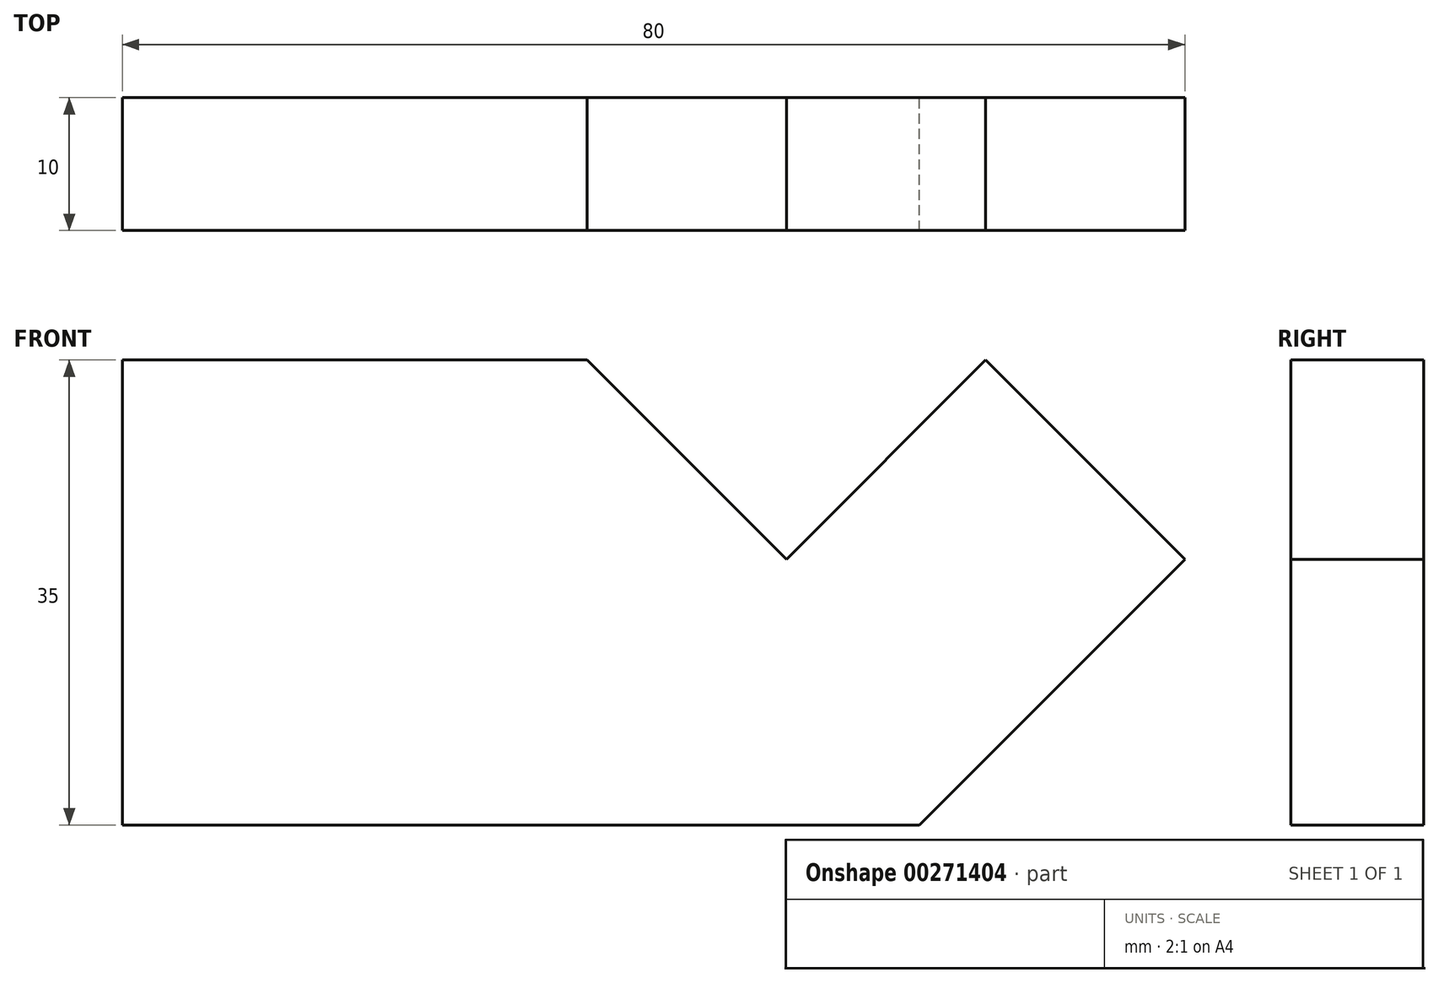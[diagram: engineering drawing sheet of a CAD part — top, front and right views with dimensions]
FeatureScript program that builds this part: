
annotation { "Feature Type Name" : "Feature", "Feature Type Description" : "" }
export const myFeature = defineFeature(function(context is Context, id is Id, definition is map)
    precondition{}
    {
        {
            var Q0;
            Q0=qCreatedBy(makeId("Front.planeOp"),FACE);
            var sketch = newSketch(context, id + "F0", { "sketchPlane" : qUnion([Q0])});
            skLineSegment(sketch, "E0", {"start": v(0, 0) * mm, "end": v(0, 35) * mm});
            skLineSegment(sketch, "E1", {"start": v(0, 0) * mm, "end": v(60, 0) * mm});
            skLineSegment(sketch, "E2", {"start": v(60, 0) * mm, "end": v(80, 20) * mm});
            skLineSegment(sketch, "E3", {"start": v(80, 20) * mm, "end": v(65, 35) * mm});
            skLineSegment(sketch, "E4", {"start": v(65, 35) * mm, "end": v(50, 20) * mm});
            skLineSegment(sketch, "E5", {"start": v(0, 35) * mm, "end": v(35, 35) * mm});
            skLineSegment(sketch, "E6", {"start": v(35, 35) * mm, "end": v(50, 20) * mm});
            skSolve(sketch);
        }
        {
            var Q0;
            Q0=makeQuery(id+"F0.imprint","IMPRINT",FACE,{"disambiguationData":[TD([[makeQuery(id+"F0.imprint","IMPRINT",EDGE,{"derivedFrom":sQuery(id+"F0.wireOp",EDGE,"E0")}),-1.0]])]});
            extrude(context, id + "F1", {"entities" : qUnion([Q0]), "depth" : 10 * mm});
        }
    });
